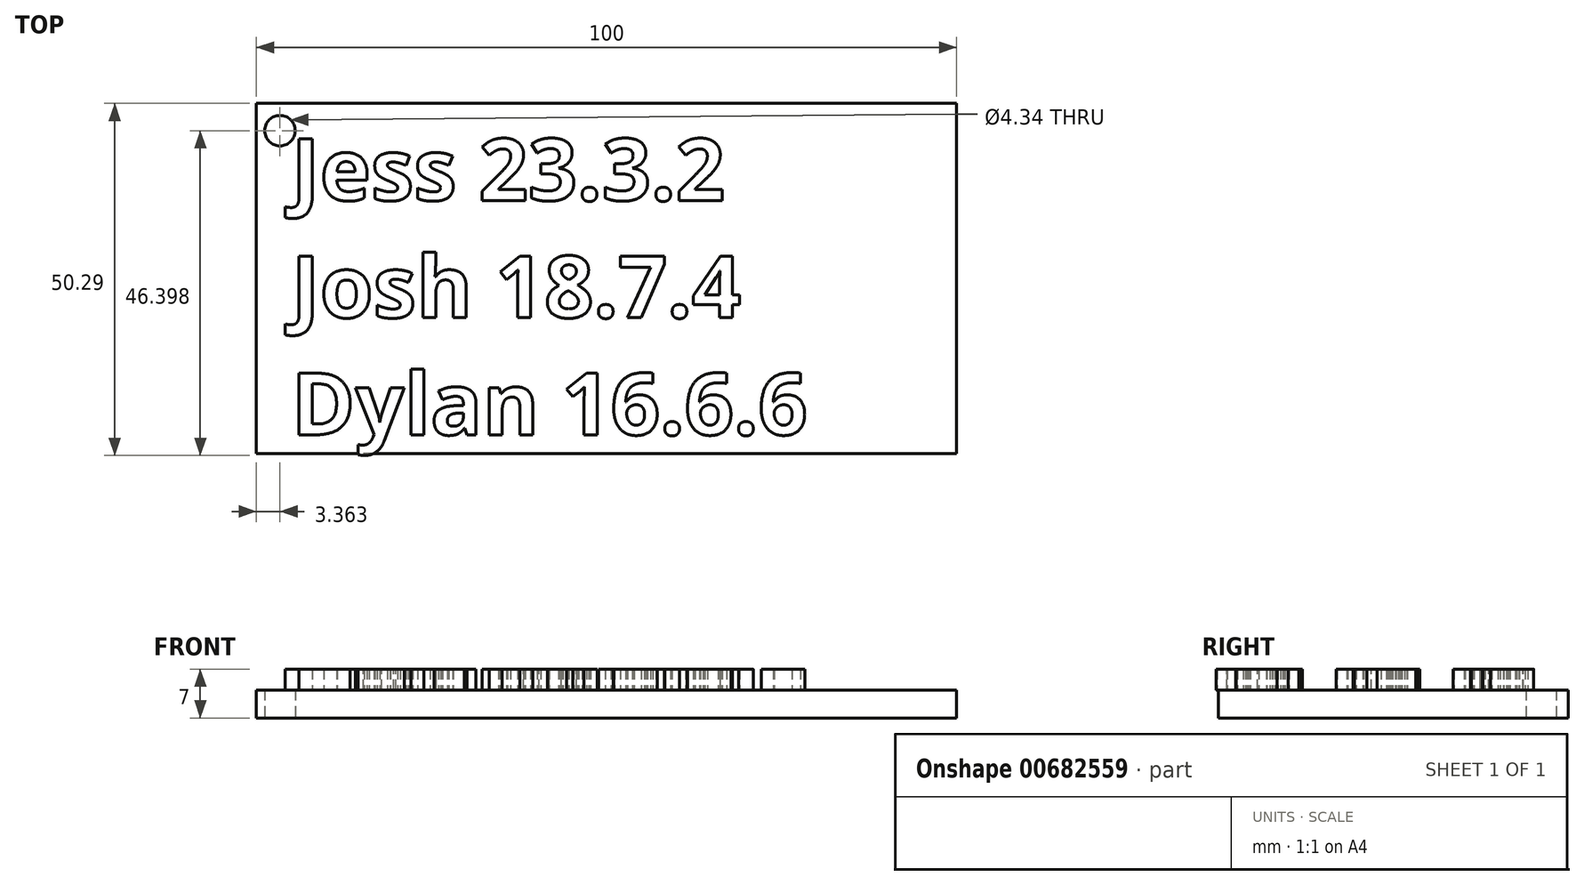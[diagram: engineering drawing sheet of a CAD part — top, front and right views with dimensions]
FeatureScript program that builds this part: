
annotation { "Feature Type Name" : "Feature", "Feature Type Description" : "" }
export const myFeature = defineFeature(function(context is Context, id is Id, definition is map)
    precondition{}
    {
        {
            var Q0;
            Q0=qCreatedBy(makeId("Top.planeOp"),FACE);
            var sketch = newSketch(context, id + "F0", { "sketchPlane" : qUnion([Q0])});
            skLineSegment(sketch, "E0.bottom", {"start": v(50, 25) * mm, "end": v(-50, 25) * mm});
            skLineSegment(sketch, "E0.top", {"start": v(50, -25) * mm, "end": v(-50, -25) * mm});
            skLineSegment(sketch, "E0.left", {"start": v(50, 25) * mm, "end": v(50, -25) * mm});
            skLineSegment(sketch, "E0.right", {"start": v(-50, 25) * mm, "end": v(-50, -25) * mm});
            skPoint(sketch, "E0.middle", {"position": v(0, 0) * mm});
            skCircle(sketch, "E1", {"center": v(-46.64, 21.1) * mm, "radius": 2.17 * mm});
            skSolve(sketch);
        }
        {
            var Q0;
            Q0=makeQuery(id+"F0.imprint","IMPRINT",FACE,{"disambiguationData":[TD([[makeQuery(id+"F0.imprint","IMPRINT",EDGE,{"derivedFrom":sQuery(id+"F0.wireOp",EDGE,"E0.bottom")}),1.0]])]});
            extrude(context, id + "F1", {"entities" : qUnion([Q0]), "depth" : 4 * mm, "offsetDistance" : 25 * mm});
        }
        {
            var Q0;
            Q0=makeQuery(id+"F1.opExtrude","CAP_FACE",FACE,{"disambiguationData":[OSD([sQuery(id+"F0.wireOp",EDGE,"E0.bottom"),sQuery(id+"F0.wireOp",EDGE,"E0.top"),sQuery(id+"F0.wireOp",EDGE,"E0.left"),sQuery(id+"F0.wireOp",EDGE,"E0.right"),sQuery(id+"F0.wireOp",EDGE,"E1")])],"isStart":false});
            var sketch = newSketch(context, id + "F2", { "sketchPlane" : qUnion([Q0])});
            skText(sketch, "E2", { "text": "Jess 23.3.2\nJosh 18.7.4\nDylan 16.6.6", "fontName": "OpenSans-Bold.ttf"});
            const initialGuessF2  = {"E2": [-0.045, 0.01114, 1, 0, 0.00886]};
            skSetInitialGuess(sketch, initialGuessF2);
            skSolve(sketch);
        }
        {
            var Q0;
            Q0 = qSketchRegion(id + "F2", true);
            extrude(context, id + "F3", {"entities" : qUnion([Q0]), "operationType" : NewBodyOperationType.ADD, "depth" : 3 * mm, "offsetDistance" : 25 * mm});
        }
    });
